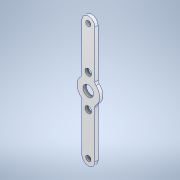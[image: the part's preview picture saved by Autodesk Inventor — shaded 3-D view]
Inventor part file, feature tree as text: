
AUTODESK INVENTOR PART (.ipt)
format: ipt  version: 2020 (Build 240168000, 168)  size: 137,216 bytes
history: native  units: in
note: dims shown in document units (in); Inventor stores cm internally (conversion verified against a paired STEP export)
features: extrude x2, sketch x2, fillet x1
ambient origin geometry x8: Origin, YZ Plane, XZ Plane, XY Plane, X Axis, Y Axis, Z Axis, Center Point
bodies: Solid1 (feature_tree)
feature tree (5):
  extrude  "Extrusion1"  Depth=0.5in
  extrude  "Extrusion2"  Depth=0.125in
  fillet  "Fillet1"  Radius=0.875in
  sketch  "Sketch1"  dims[d0=4.5in d1=0.5in]
  sketch  "Sketch2"  dims[d2=0.196in d3=0.406in d4=0.875in d5=0.125in d6=0.0in d7=1.25in d8=0.25in d9=0.25in d10=0.0in d11=0.0in d12=0.125in]
